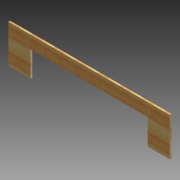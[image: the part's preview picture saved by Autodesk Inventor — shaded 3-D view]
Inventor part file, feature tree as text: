
AUTODESK INVENTOR PART (.ipt)
format: ipt  version: 2012 (Build 160160000, 160)  size: 82,944 bytes
history: native  units: in
note: dims shown in document units (in); Inventor stores cm internally (conversion verified against a paired STEP export)
features: extrude x1, sketch x1
ambient origin geometry x8: Origin, YZ Plane, XZ Plane, XY Plane, X Axis, Y Axis, Z Axis, Center Point
bodies: Solid1 (feature_tree)
feature tree (2):
  extrude  "Extrusion1"  Depth=9.0in
  sketch  "Sketch1"  dims[d0=37.875in d1=9.0in d2=27.5in d3=5.1875in d4=5.1875in d5=3.0in d6=0.4375in d7=0.0in]
